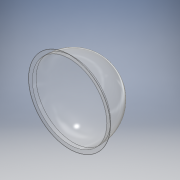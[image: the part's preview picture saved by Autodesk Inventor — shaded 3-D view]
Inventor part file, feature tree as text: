
AUTODESK INVENTOR PART (.ipt)
format: ipt  version: 2017 SP1 (Build 210196100, 196)  size: 171,008 bytes
history: native  units: mm
features: extrude x3, sketch x3, fillet x1, shell x1
ambient origin geometry x8: Origin, YZ Plane, XZ Plane, XY Plane, X Axis, Y Axis, Z Axis, Center Point
bodies: Solid1 (feature_tree)
feature tree (8):
  extrude  "Extrusion1"  Depth=4.0mm TaperAngle=0.0deg
  extrude  "Extrusion2"  Depth=225.0mm TaperAngle=0.0deg
  sketch  "Sketch3"  dims[d7=450.0mm d9=2.0mm d10=0.0mm d11=205.0mm d14=1.0mm]
  extrude  "Extrusion3"  Depth=2.0mm TaperAngle=0.0deg
  fillet  "Fillet2"  Radius=205.0mm
  shell  "Shell3"  Thickness=1.0mm
  sketch  "Sketch1"  dims[d0=450.0mm d1=4.0mm d2=0.0mm]
  sketch  "Sketch2"  dims[d3=410.0mm d4=225.0mm d5=0.0mm]
